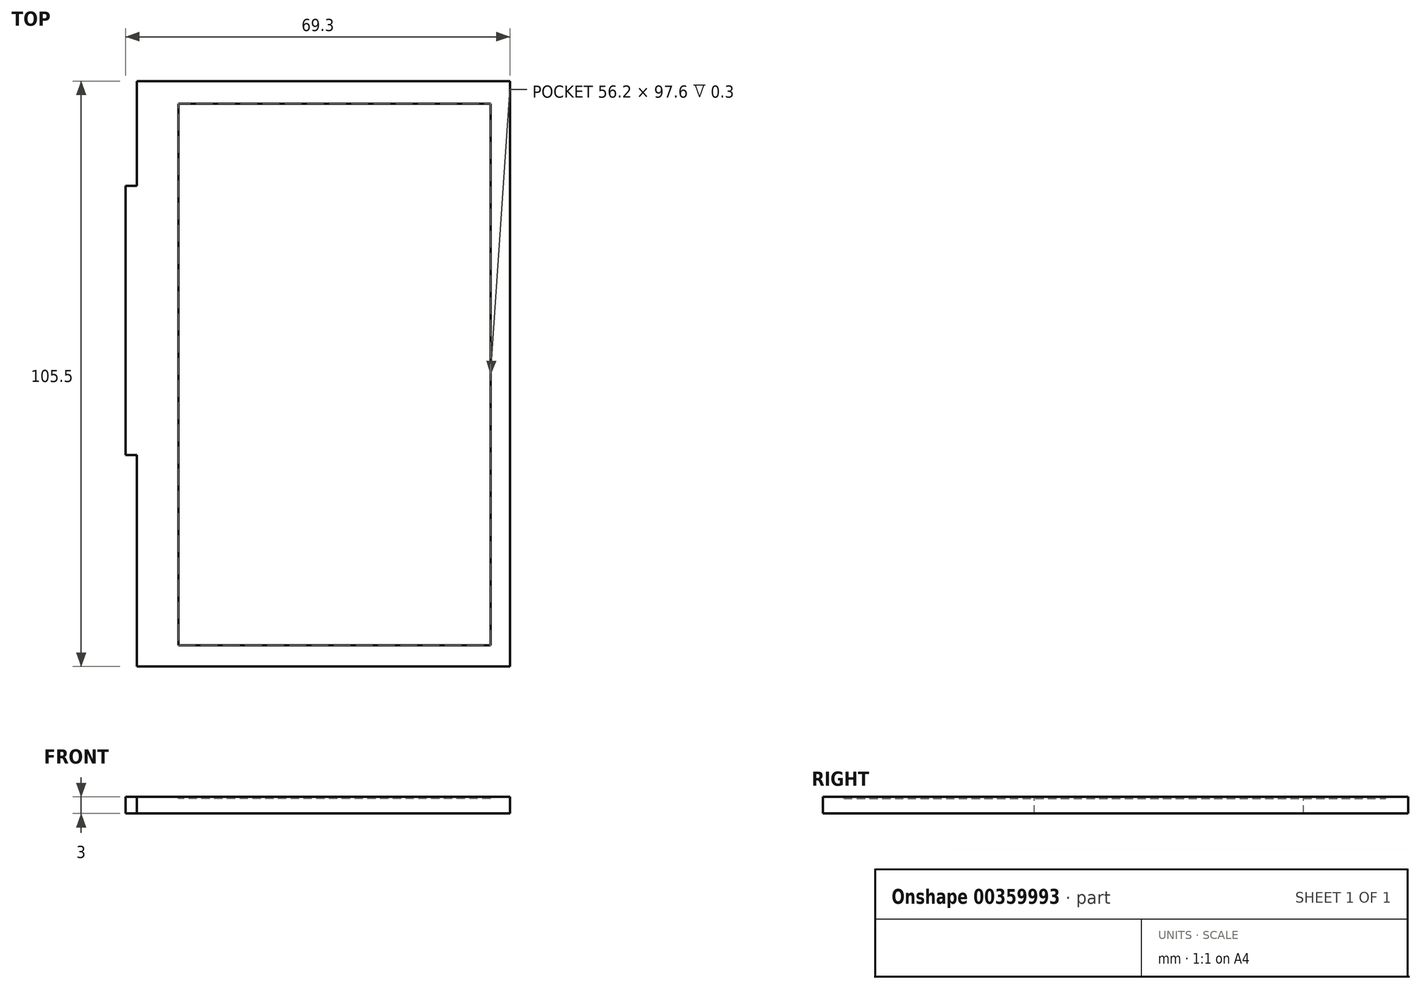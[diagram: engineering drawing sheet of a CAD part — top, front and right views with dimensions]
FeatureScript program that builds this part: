
annotation { "Feature Type Name" : "Feature", "Feature Type Description" : "" }
export const myFeature = defineFeature(function(context is Context, id is Id, definition is map)
    precondition{}
    {
        {
            var Q0;
            Q0=qCreatedBy(makeId("Top.planeOp"),FACE);
            var sketch = newSketch(context, id + "F0", { "sketchPlane" : qUnion([Q0])});
            skLineSegment(sketch, "E0.bottom", {"start": v(-22.03, -48.3) * mm, "end": v(45.27, -48.3) * mm});
            skLineSegment(sketch, "E0.top", {"start": v(-22.03, 57.2) * mm, "end": v(45.27, 57.2) * mm});
            skLineSegment(sketch, "E0.left", {"start": v(-22.03, -48.3) * mm, "end": v(-22.03, 57.2) * mm});
            skLineSegment(sketch, "E0.right", {"start": v(45.27, -48.3) * mm, "end": v(45.27, 57.2) * mm});
            skSolve(sketch);
        }
        {
            var Q0;
            Q0=makeQuery(id+"F0.imprint","IMPRINT",FACE,{"disambiguationData":[TD([[makeQuery(id+"F0.imprint","IMPRINT",EDGE,{"derivedFrom":sQuery(id+"F0.wireOp",EDGE,"E0.bottom")}),1.0]])]});
            extrude(context, id + "F1", {"entities" : qUnion([Q0]), "depth" : 3 * mm});
        }
        {
            var Q0;
            Q0=makeQuery(id+"F1.opExtrude","CAP_FACE",FACE,{"disambiguationData":[OSD([sQuery(id+"F0.wireOp",EDGE,"E0.bottom"),sQuery(id+"F0.wireOp",EDGE,"E0.top"),sQuery(id+"F0.wireOp",EDGE,"E0.left"),sQuery(id+"F0.wireOp",EDGE,"E0.right")])],"isStart":false});
            var sketch = newSketch(context, id + "F2", { "sketchPlane" : qUnion([Q0])});
            skLineSegment(sketch, "E1.bottom", {"start": v(41.72, -44.5) * mm, "end": v(-14.48, -44.5) * mm});
            skLineSegment(sketch, "E1.top", {"start": v(41.72, 53.1) * mm, "end": v(-14.48, 53.1) * mm});
            skLineSegment(sketch, "E1.left", {"start": v(41.72, -44.5) * mm, "end": v(41.72, 53.1) * mm});
            skLineSegment(sketch, "E1.right", {"start": v(-14.48, -44.5) * mm, "end": v(-14.48, 53.1) * mm});
            skSolve(sketch);
        }
        {
            var Q0;
            Q0=makeQuery(id+"F2.imprint","IMPRINT",FACE,{"disambiguationData":[TD([[makeQuery(id+"F2.imprint","IMPRINT",EDGE,{"derivedFrom":sQuery(id+"F2.wireOp",EDGE,"E1.bottom")}),-1.0]])]});
            extrude(context, id + "F3", {"entities" : qUnion([Q0]), "operationType" : NewBodyOperationType.REMOVE, "oppositeDirection" : true, "depth" : .3 * mm});
        }
        {
            var Q0;
            Q0=makeQuery(id+"F1.opExtrude","SWEPT_FACE",FACE,{"disambiguationData":[OSD([sQuery(id+"F0.wireOp",EDGE,"E0.left")])]});
            var sketch = newSketch(context, id + "F4", { "sketchPlane" : qUnion([Q0])});
            skLineSegment(sketch, "E2.bottom", {"start": v(10.2, 0) * mm, "end": v(-38.3, 0) * mm});
            skLineSegment(sketch, "E2.top", {"start": v(10.2, 3) * mm, "end": v(-38.3, 3) * mm});
            skLineSegment(sketch, "E2.left", {"start": v(10.2, 0) * mm, "end": v(10.2, 3) * mm});
            skLineSegment(sketch, "E2.right", {"start": v(-38.3, 0) * mm, "end": v(-38.3, 3) * mm});
            skSolve(sketch);
        }
        {
            var Q0;
            Q0=makeQuery(id+"F4.imprint","IMPRINT",FACE,{"disambiguationData":[TD([[makeQuery(id+"F4.imprint","IMPRINT",EDGE,{"derivedFrom":sQuery(id+"F4.wireOp",EDGE,"E2.bottom")}),-1.0]])]});
            extrude(context, id + "F5", {"entities" : qUnion([Q0]), "operationType" : NewBodyOperationType.ADD, "depth" : 2 * mm});
        }
    });
